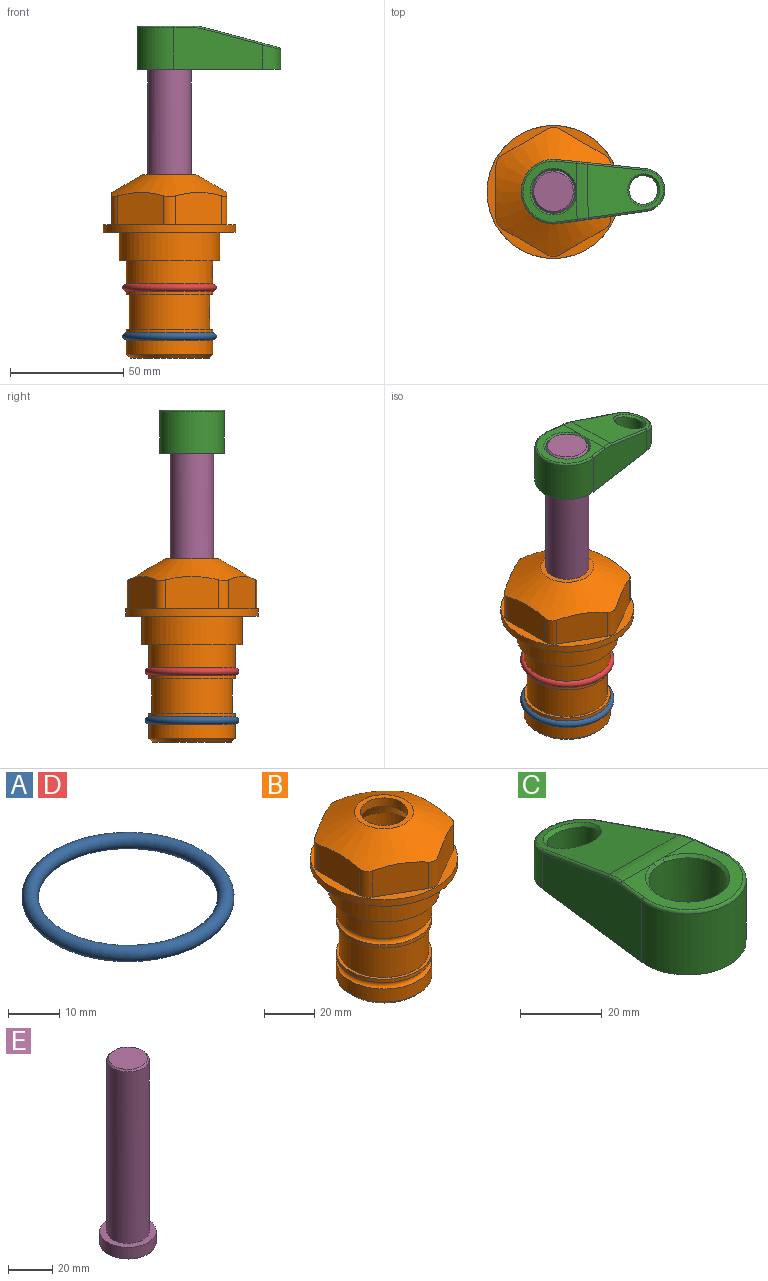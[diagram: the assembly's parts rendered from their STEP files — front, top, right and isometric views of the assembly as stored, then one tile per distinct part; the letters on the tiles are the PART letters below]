
ASSEMBLY  parts=5 mates=4
PART A: 1 faces, bbox 44.7x44.7x3.2 mm
  f0: torus R=19.05mm, axis (0,0,1), area 1193.9mm2
PART B: 36 faces, bbox 58.7x58.7x81 mm
  f0: cylinder r=17.78mm len=35.56mm, axis (0,0,1), area 1670.8mm2, adj f23,f24,f31
  f1: cylinder r=19.05mm len=38.1mm, axis (0,0,1), area 1191.9mm2, adj f26,f27,f30
  f2: plane 58.66x58.66mm, normal (0,0,-1), area 1150.6mm2, adj f3,f28
  f3: cylinder r=29.33mm len=58.66mm, axis (0,0,-1), area 585.1mm2, adj f2,f4
  f4: plane 58.66x58.66mm, normal (0,0,1), area 475.9mm2, adj f3,f5,f6,f7,f8,f9,f10,f11
  f5: plane 20.32x14.34mm, normal (-0.5,0.87,0), area 324.4mm2, adj f4,f15,f16,f17
  f6: plane 20.32x14.34mm, normal (0.5,0.87,0), area 324.4mm2, adj f4,f14,f15,f17
  f7: plane 23.48x14.34mm, normal (1,0,0), area 324.4mm2, adj f4,f13,f14,f17
  f8: plane 20.32x14.34mm, normal (0.5,-0.87,0), area 324.4mm2, adj f4,f12,f13,f17
  f9: plane 20.32x14.34mm, normal (-0.5,-0.87,0), area 324.4mm2, adj f4,f11,f12,f17
  f10: plane 23.48x14.34mm, normal (-1,0,0), area 324.4mm2, adj f4,f11,f16,f17
  f11: cylinder r=5.08mm len=12.85mm, axis (0,0,-1), area 67.2mm2, adj f4,f9,f10,f17
  f12: cylinder r=5.08mm len=12.85mm, axis (0,0,-1), area 67.2mm2, adj f4,f8,f9,f17
  f13: cylinder r=5.08mm len=12.85mm, axis (0,0,-1), area 67.2mm2, adj f4,f7,f8,f17
  f14: cylinder r=5.08mm len=12.85mm, axis (0,0,-1), area 67.2mm2, adj f4,f6,f7,f17
  f15: cylinder r=5.08mm len=12.85mm, axis (0,0,-1), area 67.2mm2, adj f4,f5,f6,f17
  f16: cylinder r=5.08mm len=12.85mm, axis (0,0,-1), area 67.2mm2, adj f4,f5,f10,f17
  f17: cone r=11.73mm half-angle=60deg, axis (0,0,-1), area 2071.8mm2, adj f5,f6,f7,f8,f9,f10,f11,f12
  f18: plane 23.46x23.46mm, normal (0,0,1), area 147.4mm2, adj f17,f35
  f19: plane 34.93x34.93mm, normal (0,0,-1), area 958mm2, adj f29
  f20: cylinder r=19.05mm len=38.1mm, axis (0,0,1), area 760.1mm2, adj f21,f29
  f21: torus R=19.05mm, axis (0,0,1), area 565.3mm2, adj f20,f22
  f22: cylinder r=19.05mm len=38.1mm, axis (0,0,1), area 190mm2, adj f21,f23
  f23: plane 38.1x38.1mm, normal (0,0,1), area 146.9mm2, adj f0,f22
  f24: plane 38.1x38.1mm, normal (0,0,-1), area 146.9mm2, adj f0,f25
  f25: cylinder r=19.05mm len=38.1mm, axis (0,0,1), area 190mm2, adj f24,f26
  f26: torus R=19.05mm, axis (0,0,1), area 565.3mm2, adj f1,f25
  f27: plane 44.45x44.45mm, normal (0,0,-1), area 411.7mm2, adj f1,f28
  f28: cylinder r=22.23mm len=44.45mm, axis (0,0,1), area 1773.5mm2, adj f2,f27
  f29: cone r=19.05mm half-angle=45deg, axis (0,0,1), area 257.5mm2, adj f19,f20
  f30: cylinder r=3.17mm len=6.75mm, axis (-1,0,0), area 128mm2, adj f1,f33
  f31: cylinder r=3.17mm len=6.35mm, axis (-1,0,0), area 102.5mm2, adj f0,f33
  f32: plane 25.4x25.4mm, normal (0,0,1), area 506.7mm2, adj f33
  f33: cylinder r=12.7mm len=66.42mm, axis (0,0,-1), area 5236.2mm2, adj f30,f31,f32,f34
  f34: cone r=9.53mm half-angle=30deg, axis (0,0,-1), area 443.4mm2, adj f33,f35
  f35: cylinder r=9.53mm len=19.05mm, axis (0,0,-1), area 240.9mm2, adj f18,f34
PART C: 31 faces, bbox 31.7x65.5x19.8 mm
  f0: plane 39.12x18.26mm, normal (0.99,0.12,0), area 612.2mm2, adj f1,f4,f7,f11,f13,f15
  f1: cylinder r=9.53mm len=18.91mm, axis (0,0,-1), area 296.1mm2, adj f0,f2,f7,f17
  f2: plane 39.12x18.26mm, normal (-0.99,0.12,0), area 612.2mm2, adj f1,f4,f7,f12,f14,f16
  f3: cylinder r=6.35mm len=12.7mm, axis (0,0,-1), area 362.4mm2, adj f7,f18
  f4: cylinder r=14.29mm len=28.58mm, axis (0,0,-1), area 882.2mm2, adj f0,f2,f7,f10
  f5: cylinder r=9.53mm len=19.05mm, axis (0,0,-1), area 1092.6mm2, adj f7,f19,f20
  f6: plane 26.99x23.69mm, normal (0,0,1), area 216.2mm2, adj f9,f10,f11,f12,f19
  f7: plane 63.5x28.58mm, normal (0,0,-1), area 661.8mm2, adj f0,f1,f2,f3,f4,f5,f22,f23
  f8: plane 33.52x23.6mm, normal (0,0.26,0.97), area 486mm2, adj f9,f15,f16,f17,f18
  f9: cylinder r=19.05mm len=24.72mm, axis (1,0,0), area 120.4mm2, adj f6,f8,f13,f14,f20
  f10: torus R=13.49mm, axis (0,0,1), area 59mm2, adj f4,f6,f11,f12
  f11: cylinder r=0.79mm len=8.67mm, axis (0.12,-0.99,0), area 10.8mm2, adj f0,f6,f10,f13
  f12: cylinder r=0.79mm len=8.67mm, axis (0.12,0.99,0), area 10.8mm2, adj f2,f6,f10,f14
  f13: bspline ~4.95x1.42mm, area 6.1mm2, adj f0,f9,f11,f15
  f14: bspline ~4.95x1.42mm, area 6.1mm2, adj f2,f9,f12,f16
  f15: cylinder r=0.79mm len=25.95mm, axis (0.12,-0.96,0.26), area 32.9mm2, adj f0,f8,f13,f17
  f16: cylinder r=0.79mm len=25.95mm, axis (0.12,0.96,-0.26), area 32.9mm2, adj f2,f8,f14,f17
  f17: bspline ~18.91x8.38mm, area 30mm2, adj f1,f8,f15,f16
  f18: bspline ~14.29x14.29mm, area 48.3mm2, adj f3,f8
  f19: cone r=9.53mm half-angle=45deg, axis (0,0,1), area 66.5mm2, adj f5,f6,f20
  f20: bspline ~3.22x0.96mm, area 3.5mm2, adj f5,f9,f19
  f21: plane 2.75x2.72mm, normal (0,0,-1), area 2.9mm2, adj f23,f25,f28
  f22: plane 23.05x15.88mm, normal (-0.99,-0.12,0), area 323.6mm2, adj f7,f25,f26,f27,f28,f29
  f23: plane 23.05x15.88mm, normal (0.99,-0.12,0), area 323.6mm2, adj f7,f21,f25,f27,f28,f30
  f24: cylinder r=9.53mm len=10.69mm, axis (0,0,-1), area 114.7mm2, adj f7,f27,f29,f30
  f25: cylinder r=12.7mm len=20.59mm, axis (0,0,-1), area 381.1mm2, adj f7,f21,f22,f23,f26,f28
  f26: plane 2.75x2.72mm, normal (0,0,-1), area 2.9mm2, adj f22,f25,f28
  f27: plane 19.72x18.37mm, normal (0,-0.26,-0.97), area 291.8mm2, adj f22,f23,f24,f28,f29,f30
  f28: cylinder r=15.88mm len=19.92mm, axis (1,0,0), area 54.8mm2, adj f21,f22,f23,f25,f26,f27
  f29: cylinder r=1.59mm len=11mm, axis (0,0,-1), area 34.7mm2, adj f7,f22,f24,f27
  f30: cylinder r=1.59mm len=11mm, axis (0,0,-1), area 34.7mm2, adj f7,f23,f24,f27
PART D: same geometry as A
PART E: 6 faces, bbox 25.4x25.4x101.6 mm
  f0: plane 17.46x17.46mm, normal (0,0,1), area 239.5mm2, adj f5
  f1: plane 25.4x25.4mm, normal (0,0,-1), area 506.7mm2, adj f2
  f2: cylinder r=12.7mm len=25.4mm, axis (0,0,1), area 506.7mm2, adj f1,f3
  f3: plane 25.4x25.4mm, normal (0,0,1), area 221.7mm2, adj f2,f4
  f4: cylinder r=9.53mm len=94.46mm, axis (0,0,1), area 5653mm2, adj f3,f5
  f5: cone r=8.73mm half-angle=45deg, axis (0,0,-1), area 64.4mm2, adj f0,f4
PLACE A t=(0,0,-21.59)mm
PLACE B at identity fixed
PLACE C rot(axis=(0,0,-1),88.9deg) t=(0,0,27.55)mm
PLACE D at identity
PLACE E rot(axis=(0,0,-1),88.9deg) t=(0,0,27.55)mm
MATE cylindrical E.f2 <-> B.f0  axis (0,0,-1) through (0,0,-10.55)mm
MATE fastened C.f4 <-> E.f2  axis (0,0,-1) through (0,0,90.26)mm
MATE fastened D.f0 <-> B.f0  axis (0,0,1) through (0,0,-24.51)mm
MATE fastened A.f0 <-> B.f0  axis (0,0,1) through (0,0,-46.1)mm
